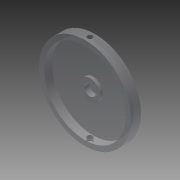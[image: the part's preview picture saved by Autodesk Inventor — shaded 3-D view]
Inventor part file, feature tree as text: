
AUTODESK INVENTOR PART (.ipt)
format: ipt  version: 2014 (Build 180170000, 170)  size: 126,976 bytes
history: native  units: mm
features: sketch x6, extrude x3, hole x3, plane x2
ambient origin geometry x8: Origin, YZ Plane, XZ Plane, XY Plane, X Axis, Y Axis, Z Axis, Center Point
bodies: Solid1 (feature_tree)
feature tree (14):
  extrude  "Extrusion1"  Depth=10.0mm TaperAngle=0.0deg
  extrude  "Extrusion2"  Depth=5.0mm TaperAngle=0.0deg
  extrude  "Extrusion3"  Depth=3.0mm TaperAngle=0.0deg
  hole  "Hole1"  [1 undecoded]
  plane  "Work Plane1"
  sketch  "Sketch5"  dims[d17=5.0mm d18=-45.0mm]
  plane  "Work Plane2"
  sketch  "Sketch6"  dims[d19=5.0mm d20=5.0mm d21=6.0mm d22=4.0mm d23=2.0mm d24=90.0deg d25=8.0mm d26=20.594885mm d27=5.0mm d28=6.0mm d29=4.0mm d30=2.0mm d31=90.0deg d32=8.0mm d33=20.594885mm]
  hole  "Hole2"  [1 undecoded]
  hole  "Hole3"  [1 undecoded]
  sketch  "Sketch1"  dims[d0=90.0mm d1=10.0mm d2=0.0mm]
  sketch  "Sketch2"  dims[d3=80.0mm d4=5.0mm d5=0.0mm]
  sketch  "Sketch3"  dims[d6=20.0mm d7=3.0mm d8=0.0mm]
  sketch  "Sketch4"  dims[d9=11.0mm d10=6.0mm d11=4.0mm d12=2.0mm d13=90.0deg d14=8.0mm d15=20.594885mm d16=45.0mm]
note: 3 required parameter values undecoded (feature->parameter linkage not recoverable at this tier; creation-order binding heuristic only, values carry confidence <= 0.55)
